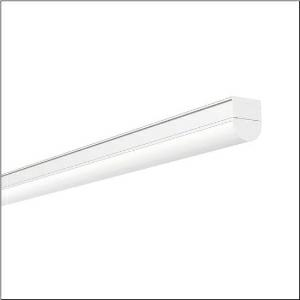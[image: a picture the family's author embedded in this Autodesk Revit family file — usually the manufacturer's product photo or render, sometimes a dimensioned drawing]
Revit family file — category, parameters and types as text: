
# Revit family: ecopack_r__31_51lj12dkm40a_26af
name_source: partatom
category: Lighting Fixtures
units: mm (PartAtom-declared; Revit-internal decimal feet)

## family parameters
Cut with Voids When Loaded = No
Host = Face
Light Source = No
Part Type = Normal
Room Calculation Point = No
Round Connector Dimension = Use Diameter
Shared = No

## types (1)
- --- (1 x LED, 4290 lm, 33 W, 5000K)
    Apparent Load = 33 VA
    CIE Flux Codes = 39 67 87 89 100
    Color Rendering = 80
    Color Temperature = 5000K
    Default Elevation = 1800 mm
    Description = Ecopack® 31, diffuser luminaire, primary optical cover: cover, of PC, frosted, light emission: direct distribution, primary light characteristic: symmetric, installation type: surface-mounted, LED, rated luminous flux: 4.300lm, luminous efficacy: 130lm/W, light colour: 830/840/850, colour temperature: 3000/4000/5000K, control gear: ECG DALI, with terminal, 5-pole, mains connection: 220..240V, AC, 50/60Hz, rated input power: 33W, housing, of aluminium, traffic white (RAL 9016), length: 1.149mm, width: 56mm, height: 68mm, end cap, of PC, white, protection rating (complete): IP20, insulation class (complete): insulation class I (protective earthing), certification: CE, impact resistance: IK06, permissible operating ambient temperature: -20..+40°C, packaging unit: 1 piece
    Height = 68 mm
    Lamp = 1 x LED
    Lamp Light Flux = 4290 lm
    Lamp Power = 33 W
    Lamp count = 1
    Length = 1149 mm
    Luminous efficacy = 130 lm/W
    Manufacturer = Siteco
    ModVariant = No
    Model = 51LJ12DKM40A
    Mounting Place = Ceiling
    Mounting Type = Surface mounted
    Number of Poles = 1
    OnlyDefault = Yes
    Power Factor = 1
    Product Name = Ecopack® 31
    Product group = diffuser luminaire
    ProductGroupID = 303
    Protection Class = Protection class I
    Protection Degree = IP 20
    RLX_Detail_Level = 1
    RlxData = <blob elided: 24909 chars, md5=3cc32dad>
    Socket = socket
    Standby Power = 0 W
    System Light Flux = 4290 lm
    System Power = 33 W
    Type Comments = individual setting: colour temperature 5000K
    Type Image = l_1007030.jpg
    URL = http://relux.com
    VarID = @adj_086325
    Voltage = 0 V
    Weight = 0.00 kg
    Width = 56 mm

## geometry (parser evidence)
native form markers: Blend x4, Sweep x15
no freeform markers — native parametric forms only
